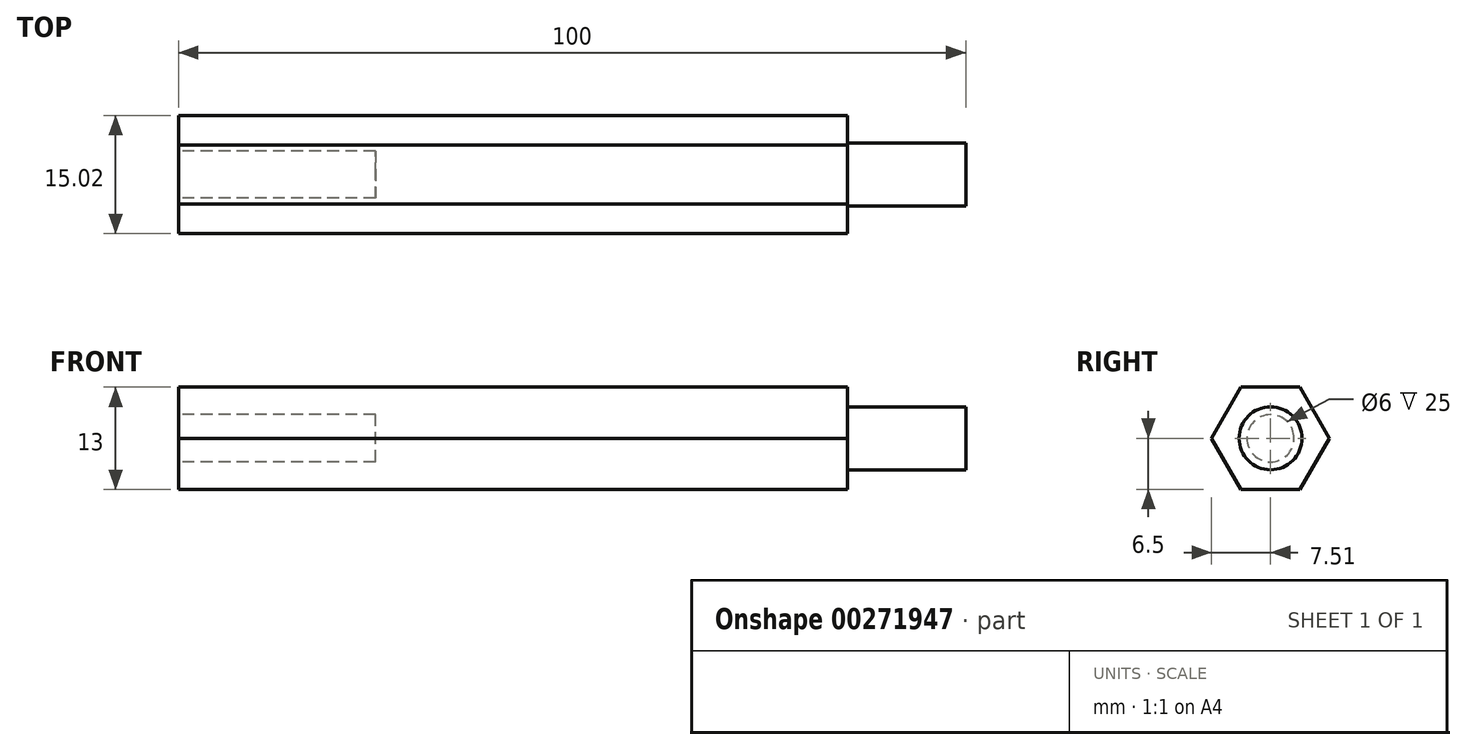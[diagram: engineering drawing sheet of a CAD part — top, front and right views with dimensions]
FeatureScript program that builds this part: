
annotation { "Feature Type Name" : "Feature", "Feature Type Description" : "" }
export const myFeature = defineFeature(function(context is Context, id is Id, definition is map)
    precondition{}
    {
        {
            var Q0;
            Q0=qCreatedBy(makeId("Right.planeOp"),FACE);
            var sketch = newSketch(context, id + "F0", { "sketchPlane" : qUnion([Q0])});
            skCircle(sketch, "E0", {"center": v(0, 0) * mm, "radius": 4 * mm});
            skCircle(sketch, "E1", {"center": v(0, 0) * mm, "radius": 3 * mm});
            skLineSegment(sketch, "E2.0", {"start": v(-7.5, 0) * mm, "end": v(-3.75, 6.5) * mm});
            skLineSegment(sketch, "E2.1", {"start": v(-3.75, 6.5) * mm, "end": v(3.75, 6.5) * mm});
            skLineSegment(sketch, "E2.2", {"start": v(3.75, 6.5) * mm, "end": v(7.5, 0) * mm});
            skLineSegment(sketch, "E2.3", {"start": v(7.5, 0) * mm, "end": v(3.75, -6.5) * mm});
            skLineSegment(sketch, "E2.4", {"start": v(3.75, -6.5) * mm, "end": v(-3.75, -6.5) * mm});
            skLineSegment(sketch, "E2.5", {"start": v(-3.75, -6.5) * mm, "end": v(-7.5, 0) * mm});
            skPoint(sketch, "E2.0.midPoint", {"position": v(-5.63, 3.25) * mm});
            skSolve(sketch);
        }
        {
            var Q0;
            Q0=makeQuery(id+"F0.imprint","IMPRINT",FACE,{"disambiguationData":[TD([[makeQuery(id+"F0.imprint","IMPRINT",EDGE,{"derivedFrom":sQuery(id+"F0.wireOp",EDGE,"2MfOCkoa-5UCb-iIcj-w9rW-OEseCSx1P8Ny")}),1.0]])]});
            var Q1;
            Q1=makeQuery(id+"F0.imprint","IMPRINT",FACE,{"disambiguationData":[TD([[makeQuery(id+"F0.imprint","IMPRINT",EDGE,{"derivedFrom":sQuery(id+"F0.wireOp",EDGE,"E0")}),1.0]])]});
            var Q2;
            Q2=makeQuery(id+"F0.imprint","IMPRINT",FACE,{"disambiguationData":[TD([[makeQuery(id+"F0.imprint","IMPRINT",EDGE,{"derivedFrom":sQuery(id+"F0.wireOp",EDGE,"E1")}),1.0]])]});
            var Q3;
            Q3=makeQuery(id+"F0.imprint","IMPRINT",FACE,{"disambiguationData":[TD([[makeQuery(id+"F0.imprint","IMPRINT",EDGE,{"derivedFrom":sQuery(id+"F0.wireOp",EDGE,"E0")}),-1.0]])]});
            extrude(context, id + "F1", {"entities" : qUnion([Q0, Q1, Q2, Q3]), "depth" : 85 * mm});
        }
        {
            var Q0;
            Q0=makeQuery(id+"F0.imprint","IMPRINT",FACE,{"disambiguationData":[TD([[makeQuery(id+"F0.imprint","IMPRINT",EDGE,{"derivedFrom":sQuery(id+"F0.wireOp",EDGE,"E1")}),1.0]])]});
            var Q1;
            Q1=sQuery(id+"F0.wireOp",EDGE,"E1");
            extrude(context, id + "F2", {"entities" : qUnion([Q0]), "operationType" : NewBodyOperationType.REMOVE, "surfaceEntities" : qUnion([Q1]), "depth" : 25 * mm});
        }
        {
            var Q0;
            Q0=makeQuery(id+"F0.imprint","IMPRINT",FACE,{"disambiguationData":[TD([[makeQuery(id+"F0.imprint","IMPRINT",EDGE,{"derivedFrom":sQuery(id+"F0.wireOp",EDGE,"E0")}),1.0]])]});
            var Q1;
            Q1=makeQuery(id+"F0.imprint","IMPRINT",FACE,{"disambiguationData":[TD([[makeQuery(id+"F0.imprint","IMPRINT",EDGE,{"derivedFrom":sQuery(id+"F0.wireOp",EDGE,"E1")}),1.0]])]});
            var Q2;
            Q2=sQuery(id+"F0.wireOp",EDGE,"E0");
            var Q3;
            Q3=makeQuery(id+"F1.opExtrude","SWEPT_BODY",BODY,{"disambiguationData":[OSD([sQuery(id+"F0.wireOp",EDGE,"2MfOCkoa-5UCb-iIcj-w9rW-OEseCSx1P8Ny")])]});
            extrude(context, id + "F3", {"entities" : qUnion([Q0, Q1]), "operationType" : NewBodyOperationType.ADD, "surfaceEntities" : qUnion([Q2]), "endBoundEntityBody" : qUnion([Q3]), "depth" : 100 * mm, "hasSecondDirection" : true, "secondDirectionOppositeDirection" : false, "secondDirectionDepth" : 85 * mm});
        }
    });
